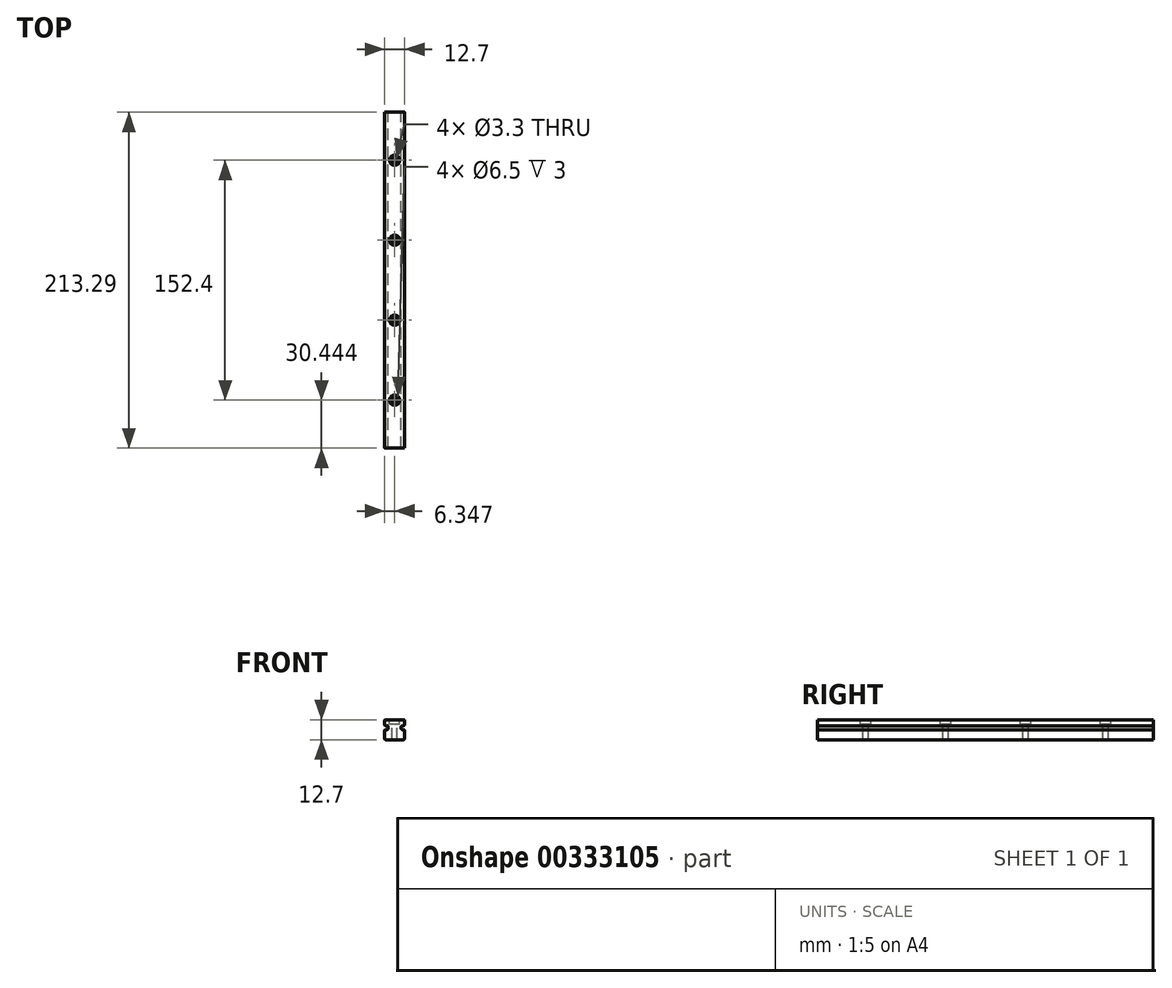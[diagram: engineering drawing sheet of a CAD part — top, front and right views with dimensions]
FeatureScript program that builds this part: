
annotation { "Feature Type Name" : "Feature", "Feature Type Description" : "" }
export const myFeature = defineFeature(function(context is Context, id is Id, definition is map)
    precondition{}
    {
        {
            var Q0;
            Q0=qCreatedBy(makeId("Front.planeOp"),FACE);
            var sketch = newSketch(context, id + "F0", { "sketchPlane" : qUnion([Q0])});
            skLineSegment(sketch, "E0", {"start": v(-9.51, 0) * mm, "end": v(3.19, 0) * mm});
            skLineSegment(sketch, "E1", {"start": v(3.19, 0) * mm, "end": v(3.19, 6.35) * mm});
            skLineSegment(sketch, "E2", {"start": v(-9.51, 0) * mm, "end": v(-9.51, 6.35) * mm});
            skLineSegment(sketch, "E3", {"start": v(3.19, 6.35) * mm, "end": v(1.02, 6.35) * mm});
            skLineSegment(sketch, "E4", {"start": v(1.02, 6.35) * mm, "end": v(1.02, 8.9) * mm});
            skLineSegment(sketch, "E5", {"start": v(1.02, 8.9) * mm, "end": v(3.19, 8.9) * mm});
            skLineSegment(sketch, "E6", {"start": v(3.19, 8.9) * mm, "end": v(3.19, 12.7) * mm});
            skLineSegment(sketch, "E7", {"start": v(3.19, 12.7) * mm, "end": v(-9.51, 12.7) * mm});
            skLineSegment(sketch, "E8", {"start": v(-9.51, 12.7) * mm, "end": v(-9.51, 8.9) * mm});
            skLineSegment(sketch, "E9", {"start": v(-9.51, 8.9) * mm, "end": v(-7.34, 8.9) * mm});
            skLineSegment(sketch, "E10", {"start": v(-7.34, 8.9) * mm, "end": v(-7.34, 6.35) * mm});
            skLineSegment(sketch, "E11", {"start": v(-7.34, 6.35) * mm, "end": v(-9.51, 6.35) * mm});
            skSolve(sketch);
        }
        {
            var Q0;
            Q0=qSketchRegion(id+"F0",true);
            extrude(context, id + "F1", {"entities" : qUnion([Q0]), "depth" : 214.3 * mm});
        }
        {
            var Q0;
            Q0=makeQuery(id+"F1.opExtrude","SWEPT_EDGE",EDGE,{"disambiguationData":[OSD([sQuery(id+"F0.wireOp",EDGE,"E5"),sQuery(id+"F0.wireOp",EDGE,"E6")])]});
            var Q1;
            Q1=makeQuery(id+"F1.opExtrude","SWEPT_EDGE",EDGE,{"disambiguationData":[OSD([sQuery(id+"F0.wireOp",EDGE,"E8"),sQuery(id+"F0.wireOp",EDGE,"E9")])]});
            var Q2;
            Q2=makeQuery(id+"F1.opExtrude","SWEPT_EDGE",EDGE,{"disambiguationData":[OSD([sQuery(id+"F0.wireOp",EDGE,"E9"),sQuery(id+"F0.wireOp",EDGE,"E10")])]});
            var Q3;
            Q3=makeQuery(id+"F1.opExtrude","SWEPT_EDGE",EDGE,{"disambiguationData":[OSD([sQuery(id+"F0.wireOp",EDGE,"E10"),sQuery(id+"F0.wireOp",EDGE,"E11")])]});
            var Q4;
            Q4=makeQuery(id+"F1.opExtrude","SWEPT_EDGE",EDGE,{"disambiguationData":[OSD([sQuery(id+"F0.wireOp",EDGE,"E2"),sQuery(id+"F0.wireOp",EDGE,"E11")])]});
            var Q5;
            Q5=makeQuery(id+"F1.opExtrude","SWEPT_EDGE",EDGE,{"disambiguationData":[OSD([sQuery(id+"F0.wireOp",EDGE,"E3"),sQuery(id+"F0.wireOp",EDGE,"E4")])]});
            var Q6;
            Q6=makeQuery(id+"F1.opExtrude","SWEPT_EDGE",EDGE,{"disambiguationData":[OSD([sQuery(id+"F0.wireOp",EDGE,"E1"),sQuery(id+"F0.wireOp",EDGE,"E3")])]});
            var Q7;
            Q7=makeQuery(id+"F1.opExtrude","SWEPT_EDGE",EDGE,{"disambiguationData":[OSD([sQuery(id+"F0.wireOp",EDGE,"E4"),sQuery(id+"F0.wireOp",EDGE,"E5")])]});
            var Q8;
            Q8=makeQuery(id+"F1.opExtrude","SWEPT_EDGE",EDGE,{"disambiguationData":[OSD([sQuery(id+"F0.wireOp",EDGE,"E6"),sQuery(id+"F0.wireOp",EDGE,"E7")])]});
            var Q9;
            Q9=makeQuery(id+"F1.opExtrude","SWEPT_EDGE",EDGE,{"disambiguationData":[OSD([sQuery(id+"F0.wireOp",EDGE,"E7"),sQuery(id+"F0.wireOp",EDGE,"E8")])]});
            var Q10;
            Q10=makeQuery(id+"F1.opExtrude","SWEPT_EDGE",EDGE,{"disambiguationData":[OSD([sQuery(id+"F0.wireOp",EDGE,"E0"),sQuery(id+"F0.wireOp",EDGE,"E2")])]});
            var Q11;
            Q11=makeQuery(id+"F1.opExtrude","SWEPT_EDGE",EDGE,{"disambiguationData":[OSD([sQuery(id+"F0.wireOp",EDGE,"E0"),sQuery(id+"F0.wireOp",EDGE,"E1")])]});
            fillet(context, id + "F2", {"entities" : qUnion([Q0, Q1, Q2, Q3, Q4, Q5, Q6, Q7, Q8, Q9, Q10, Q11]), "radius" : 0.64 * mm, "tangentPropagation" : true, "allowEdgeOverflow" : false});
        }
        {
            var Q0;
            Q0=makeQuery(id+"F1.opExtrude","SWEPT_FACE",FACE,{"disambiguationData":[OSD([sQuery(id+"F0.wireOp",EDGE,"E7")])]});
            var sketch = newSketch(context, id + "F3", { "sketchPlane" : qUnion([Q0])});
            skPoint(sketch, "E12", {"position": v(-3.16, -30.96) * mm});
            skPoint(sketch, "E13", {"position": v(-3.16, -81.76) * mm});
            skPoint(sketch, "E14", {"position": v(-3.16, -132.56) * mm});
            skPoint(sketch, "E15", {"position": v(-3.16, -183.36) * mm});
            skLineSegment(sketch, "E16", {"start": v(-8.88, -107.16) * mm, "end": v(-5.87, -107.16) * mm, "construction": true});
            skLineSegment(sketch, "E17", {"start": v(-3.16, 0) * mm, "end": v(-3.16, -5.12) * mm, "construction": true});
            skSolve(sketch);
        }
        {
            var Q0;
            Q0=sQuery(id+"F3.wireOp",VERTEX,"E12");
            var Q1;
            Q1=sQuery(id+"F3.wireOp",VERTEX,"E13");
            var Q2;
            Q2=sQuery(id+"F3.wireOp",VERTEX,"E14");
            var Q3;
            Q3=sQuery(id+"F3.wireOp",VERTEX,"E15");
            var Q4;
            Q4=makeQuery(id+"F1.opExtrude","SWEPT_BODY",BODY,{"disambiguationData":[OSD([sQuery(id+"F0.wireOp",EDGE,"E0"),sQuery(id+"F0.wireOp",EDGE,"E1"),sQuery(id+"F0.wireOp",EDGE,"E2"),sQuery(id+"F0.wireOp",EDGE,"E3"),sQuery(id+"F0.wireOp",EDGE,"E4"),sQuery(id+"F0.wireOp",EDGE,"E5"),sQuery(id+"F0.wireOp",EDGE,"E6"),sQuery(id+"F0.wireOp",EDGE,"E7"),sQuery(id+"F0.wireOp",EDGE,"E8"),sQuery(id+"F0.wireOp",EDGE,"E9"),sQuery(id+"F0.wireOp",EDGE,"E10"),sQuery(id+"F0.wireOp",EDGE,"E11")])]});
            hole(context, id + "F4", {"style" : HoleStyle.C_BORE, "endStyle" : HoleEndStyle.BLIND, "standardTappedOrClearance" : lookupTablePath({ "standard" : "ISO", "fit" : "Normal", "size" : "M3", "type" : "Clearance" }), "standardBlindInLast" : lookupTablePath({ "fit" : "Standard", "standard" : "ISO", "size" : "M3", "type" : "Clearance" }), "holeDiameter" : 3.3 * mm, "cBoreDiameter" : 6.5 * mm, "cBoreDepth" : 3 * mm, "holeDepth" : 14.5 * mm, "tappedDepth" : 12.7 * mm, "tapClearance" : 3, "locations" : qUnion([Q0, Q1, Q2, Q3]), "scope" : qUnion([Q4])});
        }
        {
            var Q0;
            Q0=makeQuery(id+"F1.opExtrude","CAP_FACE",FACE,{"disambiguationData":[OSD([sQuery(id+"F0.wireOp",EDGE,"E0"),sQuery(id+"F0.wireOp",EDGE,"E1"),sQuery(id+"F0.wireOp",EDGE,"E2"),sQuery(id+"F0.wireOp",EDGE,"E3"),sQuery(id+"F0.wireOp",EDGE,"E4"),sQuery(id+"F0.wireOp",EDGE,"E5"),sQuery(id+"F0.wireOp",EDGE,"E6"),sQuery(id+"F0.wireOp",EDGE,"E7"),sQuery(id+"F0.wireOp",EDGE,"E8"),sQuery(id+"F0.wireOp",EDGE,"E9"),sQuery(id+"F0.wireOp",EDGE,"E10"),sQuery(id+"F0.wireOp",EDGE,"E11")])],"isStart":false});
            extrude(context, id + "F5", {"entities" : qUnion([Q0]), "operationType" : NewBodyOperationType.REMOVE, "oppositeDirection" : true, "depth" : 0.5 * mm});
        }
        {
            var Q0;
            Q0=makeQuery(id+"F1.opExtrude","CAP_FACE",FACE,{"disambiguationData":[OSD([sQuery(id+"F0.wireOp",EDGE,"E0"),sQuery(id+"F0.wireOp",EDGE,"E1"),sQuery(id+"F0.wireOp",EDGE,"E2"),sQuery(id+"F0.wireOp",EDGE,"E3"),sQuery(id+"F0.wireOp",EDGE,"E4"),sQuery(id+"F0.wireOp",EDGE,"E5"),sQuery(id+"F0.wireOp",EDGE,"E6"),sQuery(id+"F0.wireOp",EDGE,"E7"),sQuery(id+"F0.wireOp",EDGE,"E8"),sQuery(id+"F0.wireOp",EDGE,"E9"),sQuery(id+"F0.wireOp",EDGE,"E10"),sQuery(id+"F0.wireOp",EDGE,"E11")])],"isStart":true});
            extrude(context, id + "F6", {"entities" : qUnion([Q0]), "operationType" : NewBodyOperationType.REMOVE, "oppositeDirection" : true, "depth" : 0.5 * mm});
        }
    });
